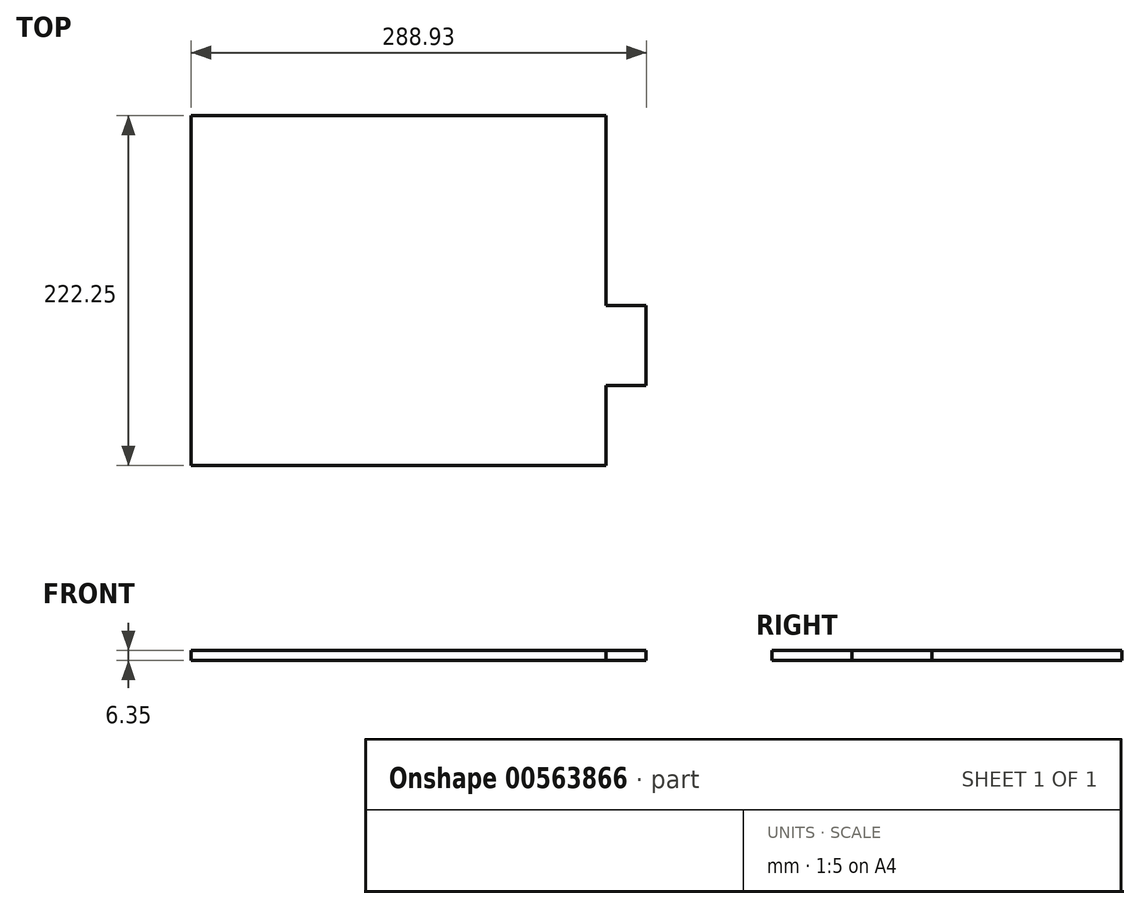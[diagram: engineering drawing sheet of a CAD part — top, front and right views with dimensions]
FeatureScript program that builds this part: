
annotation { "Feature Type Name" : "Feature", "Feature Type Description" : "" }
export const myFeature = defineFeature(function(context is Context, id is Id, definition is map)
    precondition{}
    {
        {
            var Q0;
            Q0=qCreatedBy(makeId("Top.planeOp"),FACE);
            var sketch = newSketch(context, id + "F0", { "sketchPlane" : qUnion([Q0])});
            skLineSegment(sketch, "E0", {"start": v(0, 0) * mm, "end": v(263.53, 0) * mm});
            skLineSegment(sketch, "E1", {"start": v(263.53, 0) * mm, "end": v(263.53, 50.8) * mm});
            skLineSegment(sketch, "E2", {"start": v(0, 0) * mm, "end": v(0, 222.25) * mm});
            skLineSegment(sketch, "E3", {"start": v(263.53, 50.8) * mm, "end": v(288.93, 50.8) * mm});
            skLineSegment(sketch, "E4", {"start": v(288.93, 50.8) * mm, "end": v(288.93, 101.6) * mm});
            skLineSegment(sketch, "E5", {"start": v(288.93, 101.6) * mm, "end": v(263.53, 101.6) * mm});
            skLineSegment(sketch, "E6", {"start": v(0, 222.25) * mm, "end": v(263.53, 222.25) * mm});
            skLineSegment(sketch, "E7", {"start": v(263.53, 222.25) * mm, "end": v(263.53, 101.6) * mm});
            skSolve(sketch);
        }
        {
            var Q0;
            Q0 = qSketchRegion(id + "F0", true);
            extrude(context, id + "F1", {"entities" : qUnion([Q0]), "depth" : 6.35 * mm, "offsetDistance" : 25.4 * mm});
        }
    });
